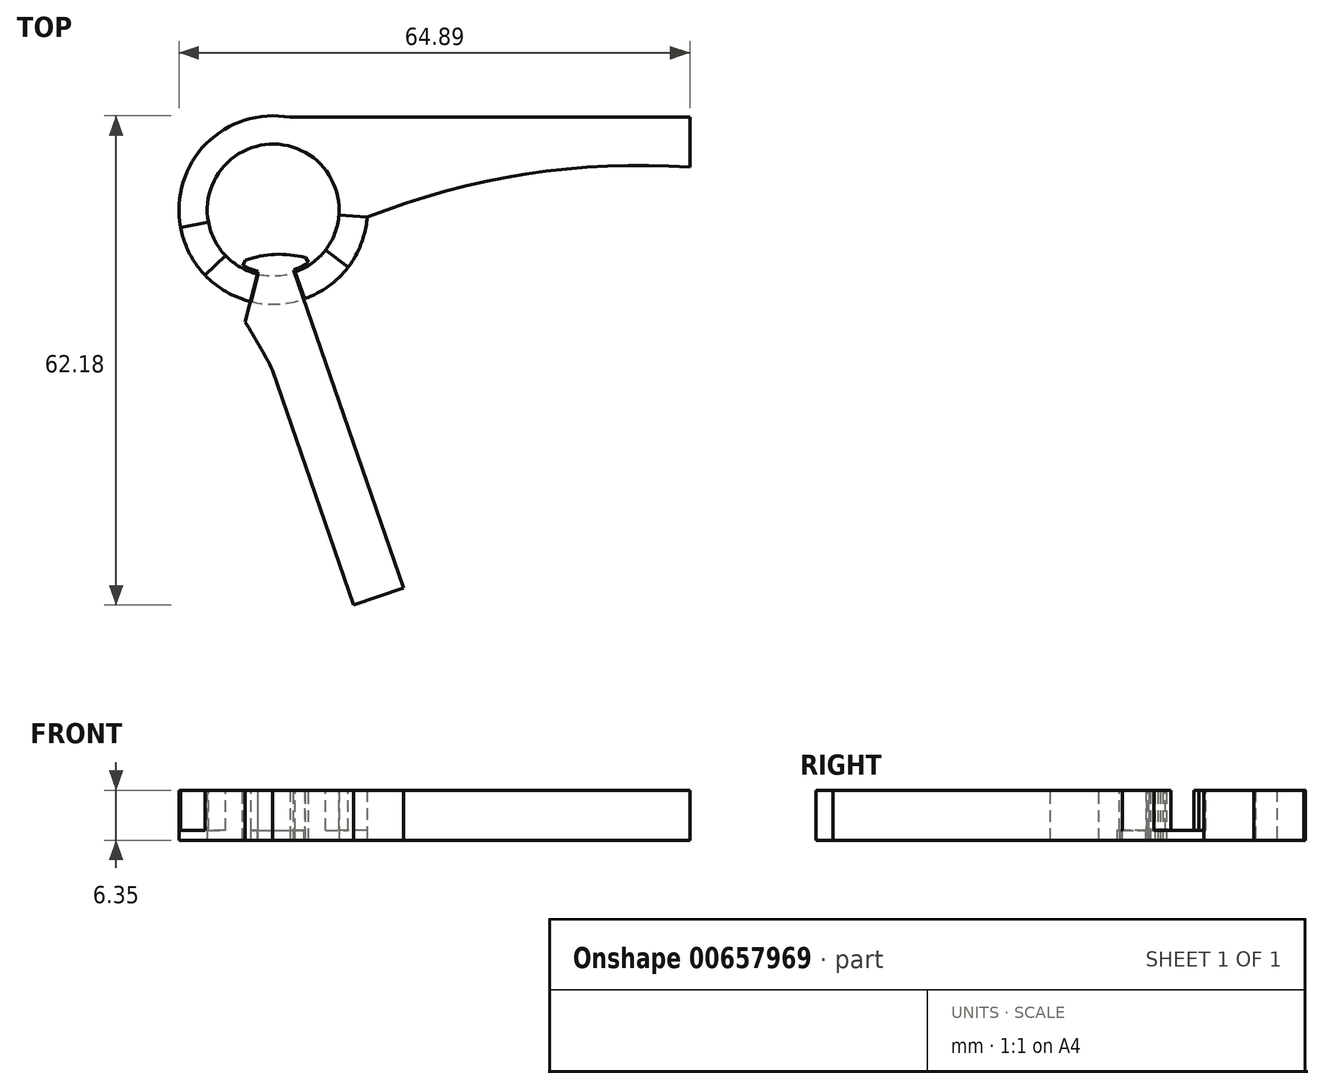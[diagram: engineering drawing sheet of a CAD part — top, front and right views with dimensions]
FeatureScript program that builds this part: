
annotation { "Feature Type Name" : "Feature", "Feature Type Description" : "" }
export const myFeature = defineFeature(function(context is Context, id is Id, definition is map)
    precondition{}
    {
        {
            var Q0;
            Q0=qCreatedBy(makeId("Top.planeOp"),FACE);
            var sketch = newSketch(context, id + "F0", { "sketchPlane" : qUnion([Q0])});
            skLineSegment(sketch, "E0", {"start": v(0, 7.8) * mm, "end": v(50.8, 7.8) * mm});
            skLineSegment(sketch, "E1", {"start": v(50.8, 7.8) * mm, "end": v(50.8, 1.45) * mm});
            skPoint(sketch, "E2.start.orphan", {"position": v(0, 1.45) * mm});
            skPoint(sketch, "E3.end.orphan", {"position": v(-12.8, 7.8) * mm});
            skArc(sketch, "E4", {"start": v(0, 7.8) * mm, "mid": v(-11.6, -11.3) * mm, "end": v(9.81, -4.9) * mm});
            skPoint(sketch, "E4.third.point", {"position": v(-11.29, -11.69) * mm});
            skArc(sketch, "E5", {"start": v(50.8, 1.45) * mm, "mid": v(29.95, 0.58) * mm, "end": v(9.81, -4.9) * mm});
            skPoint(sketch, "E6.orphan", {"position": v(50.8, -4.9) * mm});
            skPoint(sketch, "E7.end.orphan", {"position": v(0, -4.9) * mm});
            skCircle(sketch, "E8", {"center": v(-2.12, -3.98) * mm, "radius": 8.37 * mm});
            skSolve(sketch);
        }
        {
            var Q0;
            Q0=makeQuery(id+"F0.imprint","IMPRINT",FACE,{"disambiguationData":[TD([[makeQuery(id+"F0.imprint","IMPRINT",EDGE,{"derivedFrom":sQuery(id+"F0.wireOp",EDGE,"E0")}),-1.0]])]});
            extrude(context, id + "F1", {"entities" : qUnion([Q0]), "depth" : 6.35 * mm, "offsetDistance" : 25.4 * mm});
        }
        {
            var Q0;
            Q0=makeQuery(id+"F1.opExtrude","CAP_FACE",FACE,{"disambiguationData":[OSD([sQuery(id+"F0.wireOp",EDGE,"E0"),sQuery(id+"F0.wireOp",EDGE,"E1"),sQuery(id+"F0.wireOp",EDGE,"E4"),sQuery(id+"F0.wireOp",EDGE,"E5"),sQuery(id+"F0.wireOp",EDGE,"E8")])],"isStart":false});
            var sketch = newSketch(context, id + "F2", { "sketchPlane" : qUnion([Q0])});
            skCircle(sketch, "E9", {"center": v(-2.12, -3.98) * mm, "radius": 8.35 * mm});
            skCircle(sketch, "E10", {"center": v(-2.12, -3.98) * mm, "radius": 11.97 * mm});
            skLineSegment(sketch, "E11", {"start": v(9.81, -4.9) * mm, "end": v(6.2, -4.62) * mm});
            skLineSegment(sketch, "E12", {"start": v(-10.33, -5.52) * mm, "end": v(-13.9, -6.19) * mm});
            skLineSegment(sketch, "E13", {"start": v(-8.17, -9.74) * mm, "end": v(-10.8, -12.24) * mm});
            skLineSegment(sketch, "E14", {"start": v(-4.06, -12.1) * mm, "end": v(-4.9, -15.63) * mm});
            skLineSegment(sketch, "E15", {"start": v(0.68, -11.85) * mm, "end": v(1.9, -15.26) * mm});
            skLineSegment(sketch, "E16", {"start": v(4.51, -9.05) * mm, "end": v(7.39, -11.25) * mm});
            skSolve(sketch);
        }
        {
            var Q0;
            {var subQ0=sQuery(id+"F2.wireOp",EDGE,"E13");var subQ1=sQuery(id+"F2.wireOp",EDGE,"E10");var subQ2=makeQuery(id+"F2.imprint","INTERSECT",VERTEX,{"derivedFrom":[subQ1,subQ0]});Q0=makeQuery(id+"F2.imprint","IMPRINT",FACE,{"disambiguationData":[TD([[makeQuery(id+"F2.imprint","IMPRINT",EDGE,{"disambiguationData":[TD([[subQ2,1.0]])],"derivedFrom":subQ1}),1.0]])]});}
            var Q1;
            {var subQ0=sQuery(id+"F2.wireOp",EDGE,"E14");var subQ1=sQuery(id+"F2.wireOp",EDGE,"E10");var subQ2=makeQuery(id+"F2.imprint","INTERSECT",VERTEX,{"derivedFrom":[subQ1,subQ0]});Q1=makeQuery(id+"F2.imprint","IMPRINT",FACE,{"disambiguationData":[TD([[makeQuery(id+"F2.imprint","IMPRINT",EDGE,{"disambiguationData":[TD([[subQ2,-1.0]])],"derivedFrom":subQ1}),1.0]])]});}
            var Q2;
            {var subQ0=sQuery(id+"F2.wireOp",EDGE,"E16");var subQ1=sQuery(id+"F2.wireOp",EDGE,"E10");var subQ2=makeQuery(id+"F2.imprint","INTERSECT",VERTEX,{"derivedFrom":[subQ1,subQ0]});Q2=makeQuery(id+"F2.imprint","IMPRINT",FACE,{"disambiguationData":[TD([[makeQuery(id+"F2.imprint","IMPRINT",EDGE,{"disambiguationData":[TD([[subQ2,-1.0]])],"derivedFrom":subQ1}),1.0]])]});}
            extrude(context, id + "F3", {"entities" : qUnion([Q0, Q1, Q2]), "operationType" : NewBodyOperationType.REMOVE, "oppositeDirection" : true, "depth" : 5.08 * mm, "offsetDistance" : 25.4 * mm});
        }
        {
            var Q0;
            {var subQ0=sQuery(id+"F0.wireOp",EDGE,"E4");var subQ1=sQuery(id+"F0.wireOp",EDGE,"E1");var subQ2=sQuery(id+"F0.wireOp",EDGE,"E5");var subQ3=sQuery(id+"F0.wireOp",EDGE,"E0");var subQ4=sQuery(id+"F0.wireOp",EDGE,"E8");Q0=makeQuery(id+"F3.boolean.opBoolean","SPLIT",FACE,{"disambiguationData":[TD([makeQuery(id+"F1.opExtrude","SWEPT_FACE",FACE,{"disambiguationData":[OSD([subQ3])]})])],"derivedFrom":makeQuery(id+"F1.opExtrude","CAP_FACE",FACE,{"disambiguationData":[OSD([subQ3,subQ1,subQ0,subQ2,subQ4])],"isStart":false})});}
            var sketch = newSketch(context, id + "F4", { "sketchPlane" : qUnion([Q0])});
            skArc(sketch, "E17", {"start": v(0.5, -11.59) * mm, "mid": v(1.47, -11.18) * mm, "end": v(2.38, -10.65) * mm});
            skLineSegment(sketch, "E18", {"start": v(-4.06, -11.79) * mm, "end": v(-5.67, -18.24) * mm});
            skLineSegment(sketch, "E19", {"start": v(0.5, -11.59) * mm, "end": v(14.45, -52) * mm});
            skLineSegment(sketch, "E20", {"start": v(-5.65, -10.35) * mm, "end": v(-6.02, -11.02) * mm});
            skLineSegment(sketch, "E21", {"start": v(1.97, -10.04) * mm, "end": v(2.38, -10.65) * mm});
            skArc(sketch, "E22", {"start": v(1.97, -10.04) * mm, "mid": v(-1.86, -9.62) * mm, "end": v(-5.65, -10.35) * mm});
            skArc(sketch, "E23.trimOffspring", {"start": v(-6.02, -11.02) * mm, "mid": v(-5.06, -11.47) * mm, "end": v(-4.06, -11.79) * mm});
            skLineSegment(sketch, "E24", {"start": v(14.45, -52) * mm, "end": v(8.11, -54.2) * mm});
            skArc(sketch, "E25", {"start": v(-2.18, -24.36) * mm, "mid": v(-3.86, -21.27) * mm, "end": v(-5.67, -18.24) * mm});
            skLineSegment(sketch, "E26", {"start": v(-2.18, -24.36) * mm, "end": v(8.11, -54.2) * mm});
            skSolve(sketch);
        }
        {
            var Q0;
            Q0=makeQuery(id+"F4.imprint","IMPRINT",FACE,{"disambiguationData":[TD([[makeQuery(id+"F4.imprint","IMPRINT",EDGE,{"derivedFrom":sQuery(id+"F4.wireOp",EDGE,"E17")}),1.0]])]});
            extrude(context, id + "F5", {"entities" : qUnion([Q0]), "oppositeDirection" : true, "depth" : 6.35 * mm, "offsetDistance" : 25.4 * mm});
        }
        {
            var Q0;
            Q0=makeQuery(id+"F0.imprint","IMPRINT",FACE,{"disambiguationData":[TD([[makeQuery(id+"F0.imprint","IMPRINT",EDGE,{"derivedFrom":sQuery(id+"F0.wireOp",EDGE,"E0")}),-1.0]])]});
            var sketch = newSketch(context, id + "F6", { "sketchPlane" : qUnion([Q0])});
            skLineSegment(sketch, "E27", {"start": v(-5.02, -15.61) * mm, "end": v(-4.14, -12.1) * mm});
            skLineSegment(sketch, "E28", {"start": v(1.76, -15.34) * mm, "end": v(0.59, -11.9) * mm});
            skArc(sketch, "E29", {"start": v(-4.14, -12.1) * mm, "mid": v(-1.76, -12.34) * mm, "end": v(0.59, -11.9) * mm});
            skArc(sketch, "E30", {"start": v(-5.02, -15.61) * mm, "mid": v(-1.6, -15.95) * mm, "end": v(1.76, -15.34) * mm});
            skSolve(sketch);
        }
        {
            var Q0;
            Q0 = qSketchRegion(id + "F6", true);
            extrude(context, id + "F7", {"entities" : qUnion([Q0]), "operationType" : NewBodyOperationType.REMOVE, "depth" : 1.27 * mm, "offsetDistance" : 25.4 * mm});
        }
    });
